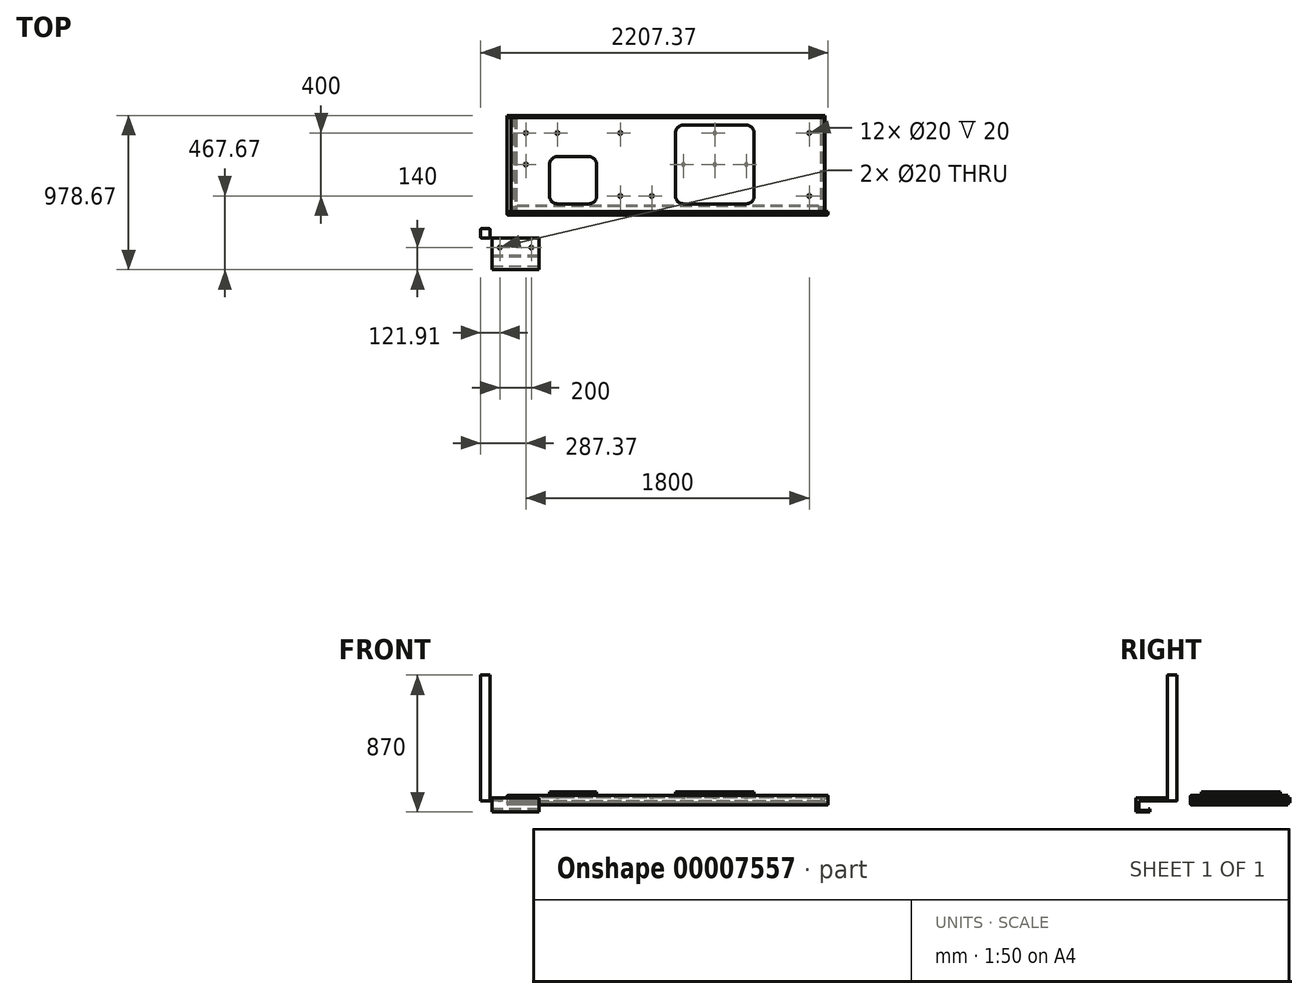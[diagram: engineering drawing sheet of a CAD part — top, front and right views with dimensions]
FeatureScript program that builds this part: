
annotation { "Feature Type Name" : "Feature", "Feature Type Description" : "" }
export const myFeature = defineFeature(function(context is Context, id is Id, definition is map)
    precondition{}
    {
        {
            var Q0;
            Q0=qCreatedBy(makeId("Top.planeOp"),FACE);
            var sketch = newSketch(context, id + "F0", { "sketchPlane" : qUnion([Q0])});
            skLineSegment(sketch, "E0.bottom", {"start": v(-63.9, 60.76) * mm, "end": v(-19.9, 60.76) * mm});
            skLineSegment(sketch, "E0.top", {"start": v(-63.9, 0.76) * mm, "end": v(-19.9, 0.76) * mm});
            skLineSegment(sketch, "E0.left", {"start": v(-71.9, 52.76) * mm, "end": v(-71.9, 8.76) * mm});
            skLineSegment(sketch, "E0.right", {"start": v(-11.9, 52.76) * mm, "end": v(-11.9, 8.76) * mm});
            skPoint(sketch, "E1.visualSharp", {"position": v(-71.9, 60.76) * mm});
            skArc(sketch, "E1.filletArc", {"start": v(-63.9, 60.76) * mm, "mid": v(-69.56, 58.42) * mm, "end": v(-71.9, 52.76) * mm});
            skPoint(sketch, "E2.visualSharp", {"position": v(-11.9, 0.76) * mm});
            skArc(sketch, "E2.filletArc", {"start": v(-19.9, 0.76) * mm, "mid": v(-14.25, 3.1) * mm, "end": v(-11.9, 8.76) * mm});
            skPoint(sketch, "E3.visualSharp", {"position": v(-71.9, 0.76) * mm});
            skArc(sketch, "E3.filletArc", {"start": v(-71.9, 8.76) * mm, "mid": v(-69.56, 3.1) * mm, "end": v(-63.9, 0.76) * mm});
            skPoint(sketch, "E4.visualSharp", {"position": v(-11.9, 60.76) * mm});
            skArc(sketch, "E4.filletArc", {"start": v(-11.9, 52.76) * mm, "mid": v(-14.25, 58.42) * mm, "end": v(-19.9, 60.76) * mm});
            skSolve(sketch);
        }
        {
            var Q0;
            Q0=makeQuery(id+"F0.imprint","IMPRINT",FACE,{"disambiguationData":[TD([[makeQuery(id+"F0.imprint","IMPRINT",EDGE,{"derivedFrom":sQuery(id+"F0.wireOp",EDGE,"E0.bottom")}),-1.0]])]});
            extrude(context, id + "F1", {"entities" : qUnion([Q0]), "depth" : 800 * mm});
        }
        {
            var Q0;
            Q0=qCreatedBy(makeId("Top.planeOp"),FACE);
            var sketch = newSketch(context, id + "F2", { "sketchPlane" : qUnion([Q0])});
            skLineSegment(sketch, "E5.bottom", {"start": v(114.46, 147.67) * mm, "end": v(2116.46, 147.67) * mm});
            skLineSegment(sketch, "E5.top", {"start": v(114.46, 787.67) * mm, "end": v(2116.46, 787.67) * mm});
            skLineSegment(sketch, "E5.left", {"start": v(114.46, 147.67) * mm, "end": v(114.46, 787.67) * mm});
            skLineSegment(sketch, "E5.right", {"start": v(2116.46, 147.67) * mm, "end": v(2116.46, 787.67) * mm});
            skSolve(sketch);
        }
        {
            var Q0;
            Q0=makeQuery(id+"F2.imprint","IMPRINT",FACE,{"disambiguationData":[TD([[makeQuery(id+"F2.imprint","IMPRINT",EDGE,{"derivedFrom":sQuery(id+"F2.wireOp",EDGE,"E5.bottom")}),1.0]])]});
            extrude(context, id + "F3", {"entities" : qUnion([Q0]), "depth" : 35 * mm});
        }
        {
            var Q0;
            Q0=makeQuery(id+"F3.opExtrude","CAP_FACE",FACE,{"disambiguationData":[OSD([sQuery(id+"F2.wireOp",EDGE,"E5.bottom"),sQuery(id+"F2.wireOp",EDGE,"E5.top"),sQuery(id+"F2.wireOp",EDGE,"E5.left"),sQuery(id+"F2.wireOp",EDGE,"E5.right")])],"isStart":false});
            var sketch = newSketch(context, id + "F4", { "sketchPlane" : qUnion([Q0])});
            skPoint(sketch, "E6", {"position": v(215.46, 267.67) * mm});
            skPoint(sketch, "E7.0.1.0", {"position": v(215.46, 467.67) * mm});
            skPoint(sketch, "E7.0.2.0", {"position": v(215.46, 667.67) * mm});
            skPoint(sketch, "E7.1.0.0", {"position": v(415.46, 267.67) * mm});
            skPoint(sketch, "E7.1.1.0", {"position": v(415.46, 467.67) * mm});
            skPoint(sketch, "E7.1.2.0", {"position": v(415.46, 667.67) * mm});
            skPoint(sketch, "E7.2.0.0", {"position": v(615.46, 267.67) * mm});
            skPoint(sketch, "E7.2.1.0", {"position": v(615.46, 467.67) * mm});
            skPoint(sketch, "E7.2.2.0", {"position": v(615.46, 667.67) * mm});
            skPoint(sketch, "E7.3.0.0", {"position": v(815.46, 267.67) * mm});
            skPoint(sketch, "E7.3.1.0", {"position": v(815.46, 467.67) * mm});
            skPoint(sketch, "E7.3.2.0", {"position": v(815.46, 667.67) * mm});
            skPoint(sketch, "E7.4.0.0", {"position": v(1015.46, 267.67) * mm});
            skPoint(sketch, "E7.4.1.0", {"position": v(1015.46, 467.67) * mm});
            skPoint(sketch, "E7.4.2.0", {"position": v(1015.46, 667.67) * mm});
            skPoint(sketch, "E7.5.0.0", {"position": v(1215.46, 267.67) * mm});
            skPoint(sketch, "E7.5.1.0", {"position": v(1215.46, 467.67) * mm});
            skPoint(sketch, "E7.5.2.0", {"position": v(1215.46, 667.67) * mm});
            skPoint(sketch, "E7.6.0.0", {"position": v(1415.46, 267.67) * mm});
            skPoint(sketch, "E7.6.1.0", {"position": v(1415.46, 467.67) * mm});
            skPoint(sketch, "E7.6.2.0", {"position": v(1415.46, 667.67) * mm});
            skPoint(sketch, "E7.7.0.0", {"position": v(1615.46, 267.67) * mm});
            skPoint(sketch, "E7.7.1.0", {"position": v(1615.46, 467.67) * mm});
            skPoint(sketch, "E7.7.2.0", {"position": v(1615.46, 667.67) * mm});
            skPoint(sketch, "E7.8.0.0", {"position": v(1815.46, 267.67) * mm});
            skPoint(sketch, "E7.8.1.0", {"position": v(1815.46, 467.67) * mm});
            skPoint(sketch, "E7.8.2.0", {"position": v(1815.46, 667.67) * mm});
            skPoint(sketch, "E7.9.0.0", {"position": v(2015.46, 267.67) * mm});
            skPoint(sketch, "E7.9.1.0", {"position": v(2015.46, 467.67) * mm});
            skPoint(sketch, "E7.9.2.0", {"position": v(2015.46, 667.67) * mm});
            skLineSegment(sketch, "E7.direction1", {"start": v(215.46, 267.67) * mm, "end": v(415.46, 267.67) * mm, "construction": true});
            skLineSegment(sketch, "E7.direction2", {"start": v(215.46, 267.67) * mm, "end": v(215.46, 467.67) * mm, "construction": true});
            skCircle(sketch, "E8", {"center": v(415.46, 467.67) * mm, "radius": 10 * mm});
            skCircle(sketch, "E9", {"center": v(615.46, 467.67) * mm, "radius": 10 * mm});
            skCircle(sketch, "E10", {"center": v(415.46, 267.67) * mm, "radius": 10 * mm});
            skCircle(sketch, "E11", {"center": v(615.46, 267.67) * mm, "radius": 10 * mm});
            skPoint(sketch, "E12.0.0.3", {"position": v(215.46, 867.67) * mm});
            skPoint(sketch, "E12.0.1.3", {"position": v(415.46, 867.67) * mm});
            skPoint(sketch, "E12.0.2.3", {"position": v(615.46, 867.67) * mm});
            skPoint(sketch, "E12.0.3.3", {"position": v(815.46, 867.67) * mm});
            skPoint(sketch, "E12.0.4.3", {"position": v(1015.46, 867.67) * mm});
            skPoint(sketch, "E12.0.5.3", {"position": v(1215.46, 867.67) * mm});
            skPoint(sketch, "E12.0.6.3", {"position": v(1415.46, 867.67) * mm});
            skPoint(sketch, "E12.0.7.3", {"position": v(1615.46, 867.67) * mm});
            skPoint(sketch, "E12.0.8.3", {"position": v(1815.46, 867.67) * mm});
            skPoint(sketch, "E12.0.9.3", {"position": v(2015.46, 867.67) * mm});
            skCircle(sketch, "E13", {"center": v(415.46, 867.67) * mm, "radius": 10 * mm});
            skCircle(sketch, "E14", {"center": v(815.46, 267.67) * mm, "radius": 10 * mm});
            skCircle(sketch, "E15", {"center": v(815.46, 667.67) * mm, "radius": 10 * mm});
            skCircle(sketch, "E16", {"center": v(1215.46, 667.67) * mm, "radius": 10 * mm});
            skCircle(sketch, "E17", {"center": v(1215.46, 267.67) * mm, "radius": 10 * mm});
            skCircle(sketch, "E18", {"center": v(1215.46, 467.67) * mm, "radius": 10 * mm});
            skCircle(sketch, "E19", {"center": v(1415.46, 467.67) * mm, "radius": 10 * mm});
            skCircle(sketch, "E20", {"center": v(1615.46, 467.67) * mm, "radius": 10 * mm});
            skCircle(sketch, "E21", {"center": v(1415.46, 667.67) * mm, "radius": 10 * mm});
            skCircle(sketch, "E22", {"center": v(1615.46, 667.67) * mm, "radius": 10 * mm});
            skCircle(sketch, "E23", {"center": v(2015.46, 667.67) * mm, "radius": 10 * mm});
            skCircle(sketch, "E24", {"center": v(1615.46, 267.67) * mm, "radius": 10 * mm});
            skCircle(sketch, "E25", {"center": v(2015.46, 267.67) * mm, "radius": 10 * mm});
            skCircle(sketch, "E26", {"center": v(215.46, 667.67) * mm, "radius": 10 * mm});
            skCircle(sketch, "E27", {"center": v(215.46, 467.67) * mm, "radius": 10 * mm});
            skCircle(sketch, "E28", {"center": v(415.46, 667.67) * mm, "radius": 10 * mm});
            skCircle(sketch, "E29", {"center": v(1015.46, 267.67) * mm, "radius": 10 * mm});
            skSolve(sketch);
        }
        {
            var Q0;
            Q0 = qSketchRegion(id + "F4", true);
            extrude(context, id + "F5", {"entities" : qUnion([Q0]), "operationType" : NewBodyOperationType.REMOVE, "oppositeDirection" : true, "depth" : 20 * mm});
        }
        {
            var Q0;
            Q0=makeQuery(id+"F3.opExtrude","SWEPT_FACE",FACE,{"disambiguationData":[OSD([sQuery(id+"F2.wireOp",EDGE,"E5.bottom")])]});
            var sketch = newSketch(context, id + "F6", { "sketchPlane" : qUnion([Q0])});
            skLineSegment(sketch, "E30.bottom", {"start": v(114.46, 35) * mm, "end": v(120.46, 35) * mm});
            skLineSegment(sketch, "E30.top", {"start": v(114.46, 23) * mm, "end": v(120.46, 23) * mm});
            skLineSegment(sketch, "E30.left", {"start": v(114.46, 35) * mm, "end": v(114.46, 23) * mm});
            skLineSegment(sketch, "E30.right", {"start": v(120.46, 35) * mm, "end": v(120.46, 23) * mm});
            skLineSegment(sketch, "E31.bottom", {"start": v(114.46, 0) * mm, "end": v(120.46, 0) * mm});
            skLineSegment(sketch, "E31.top", {"start": v(114.46, 11) * mm, "end": v(120.46, 11) * mm});
            skLineSegment(sketch, "E31.left", {"start": v(114.46, 0) * mm, "end": v(114.46, 11) * mm});
            skLineSegment(sketch, "E31.right", {"start": v(120.46, 0) * mm, "end": v(120.46, 11) * mm});
            skLineSegment(sketch, "E32.bottom", {"start": v(132.46, 0) * mm, "end": v(144.46, 0) * mm});
            skLineSegment(sketch, "E32.top", {"start": v(132.46, 6) * mm, "end": v(144.46, 6) * mm});
            skLineSegment(sketch, "E32.left", {"start": v(132.46, 0) * mm, "end": v(132.46, 6) * mm});
            skLineSegment(sketch, "E32.right", {"start": v(144.46, 0) * mm, "end": v(144.46, 6) * mm});
            skLineSegment(sketch, "E33.bottom", {"start": v(2116.46, 35) * mm, "end": v(2110.46, 35) * mm});
            skLineSegment(sketch, "E33.top", {"start": v(2116.46, 23) * mm, "end": v(2110.46, 23) * mm});
            skLineSegment(sketch, "E33.left", {"start": v(2116.46, 35) * mm, "end": v(2116.46, 23) * mm});
            skLineSegment(sketch, "E33.right", {"start": v(2110.46, 35) * mm, "end": v(2110.46, 23) * mm});
            skLineSegment(sketch, "E34.bottom", {"start": v(2116.46, 0) * mm, "end": v(2110.46, 0) * mm});
            skLineSegment(sketch, "E34.top", {"start": v(2116.46, 11) * mm, "end": v(2110.46, 11) * mm});
            skLineSegment(sketch, "E34.left", {"start": v(2116.46, 0) * mm, "end": v(2116.46, 11) * mm});
            skLineSegment(sketch, "E34.right", {"start": v(2110.46, 0) * mm, "end": v(2110.46, 11) * mm});
            skLineSegment(sketch, "E35.bottom", {"start": v(2098.46, 0) * mm, "end": v(2086.46, 0) * mm});
            skLineSegment(sketch, "E35.top", {"start": v(2098.46, 6) * mm, "end": v(2086.46, 6) * mm});
            skLineSegment(sketch, "E35.left", {"start": v(2098.46, 0) * mm, "end": v(2098.46, 6) * mm});
            skLineSegment(sketch, "E35.right", {"start": v(2086.46, 0) * mm, "end": v(2086.46, 6) * mm});
            skSolve(sketch);
        }
        {
            var Q0;
            Q0 = qSketchRegion(id + "F6", true);
            extrude(context, id + "F7", {"entities" : qUnion([Q0]), "operationType" : NewBodyOperationType.REMOVE, "endBound" : BoundingType.UP_TO_NEXT, "oppositeDirection" : true, "depth" : 25 * mm});
        }
        {
            var Q0;
            Q0=makeQuery(id+"F3.opExtrude","CAP_FACE",FACE,{"disambiguationData":[OSD([sQuery(id+"F2.wireOp",EDGE,"E5.bottom"),sQuery(id+"F2.wireOp",EDGE,"E5.top"),sQuery(id+"F2.wireOp",EDGE,"E5.left"),sQuery(id+"F2.wireOp",EDGE,"E5.right")])],"isStart":false});
            var sketch = newSketch(context, id + "F8", { "sketchPlane" : qUnion([Q0])});
            skLineSegment(sketch, "E36", {"start": v(415.46, 517.67) * mm, "end": v(615.46, 517.67) * mm});
            skArc(sketch, "E37", {"start": v(615.46, 517.67) * mm, "mid": v(650.82, 503.03) * mm, "end": v(665.46, 467.67) * mm});
            skLineSegment(sketch, "E38", {"start": v(665.46, 467.67) * mm, "end": v(665.46, 267.67) * mm});
            skArc(sketch, "E39", {"start": v(665.46, 267.67) * mm, "mid": v(650.82, 232.31) * mm, "end": v(615.46, 217.67) * mm});
            skLineSegment(sketch, "E40", {"start": v(615.46, 217.67) * mm, "end": v(415.46, 217.67) * mm});
            skArc(sketch, "E41", {"start": v(415.46, 217.67) * mm, "mid": v(380.1, 232.31) * mm, "end": v(365.46, 267.67) * mm});
            skLineSegment(sketch, "E42", {"start": v(365.46, 267.67) * mm, "end": v(365.46, 467.67) * mm});
            skArc(sketch, "E43", {"start": v(365.46, 467.67) * mm, "mid": v(380.1, 503.03) * mm, "end": v(415.46, 517.67) * mm});
            skLineSegment(sketch, "E44.bottom", {"start": v(1215.46, 717.67) * mm, "end": v(1615.46, 717.67) * mm});
            skLineSegment(sketch, "E44.top", {"start": v(1215.46, 217.67) * mm, "end": v(1615.46, 217.67) * mm});
            skLineSegment(sketch, "E44.left", {"start": v(1165.46, 667.67) * mm, "end": v(1165.46, 267.67) * mm});
            skLineSegment(sketch, "E44.right", {"start": v(1665.46, 667.67) * mm, "end": v(1665.46, 267.67) * mm});
            skPoint(sketch, "E45.visualSharp", {"position": v(1165.46, 717.67) * mm});
            skArc(sketch, "E45.filletArc", {"start": v(1215.46, 717.67) * mm, "mid": v(1180.1, 703.03) * mm, "end": v(1165.46, 667.67) * mm});
            skPoint(sketch, "E46.visualSharp", {"position": v(1665.46, 717.67) * mm});
            skArc(sketch, "E46.filletArc", {"start": v(1665.46, 667.67) * mm, "mid": v(1650.82, 703.03) * mm, "end": v(1615.46, 717.67) * mm});
            skPoint(sketch, "E47.visualSharp", {"position": v(1665.46, 217.67) * mm});
            skArc(sketch, "E47.filletArc", {"start": v(1615.46, 217.67) * mm, "mid": v(1650.82, 232.31) * mm, "end": v(1665.46, 267.67) * mm});
            skPoint(sketch, "E48.visualSharp", {"position": v(1165.46, 217.67) * mm});
            skArc(sketch, "E48.filletArc", {"start": v(1165.46, 267.67) * mm, "mid": v(1180.1, 232.31) * mm, "end": v(1215.46, 217.67) * mm});
            skSolve(sketch);
        }
        {
            var Q0;
            Q0 = qSketchRegion(id + "F8", true);
            extrude(context, id + "F9", {"entities" : qUnion([Q0]), "depth" : 21 * mm});
        }
        {
            var Q0;
            Q0=makeQuery(id+"F4.imprint","IMPRINT",FACE,{"disambiguationData":[TD([[makeQuery(id+"F4.imprint","IMPRINT",EDGE,{"derivedFrom":sQuery(id+"F4.wireOp",EDGE,"E8")}),1.0]])]});
            var Q1;
            Q1=makeQuery(id+"F4.imprint","IMPRINT",FACE,{"disambiguationData":[TD([[makeQuery(id+"F4.imprint","IMPRINT",EDGE,{"derivedFrom":sQuery(id+"F4.wireOp",EDGE,"E9")}),1.0]])]});
            var Q2;
            Q2=makeQuery(id+"F4.imprint","IMPRINT",FACE,{"disambiguationData":[TD([[makeQuery(id+"F4.imprint","IMPRINT",EDGE,{"derivedFrom":sQuery(id+"F4.wireOp",EDGE,"E11")}),1.0]])]});
            var Q3;
            Q3=makeQuery(id+"F4.imprint","IMPRINT",FACE,{"disambiguationData":[TD([[makeQuery(id+"F4.imprint","IMPRINT",EDGE,{"derivedFrom":sQuery(id+"F4.wireOp",EDGE,"E10")}),1.0]])]});
            var Q4;
            Q4=makeQuery(id+"F4.imprint","IMPRINT",FACE,{"disambiguationData":[TD([[makeQuery(id+"F4.imprint","IMPRINT",EDGE,{"derivedFrom":sQuery(id+"F4.wireOp",EDGE,"E16")}),1.0]])]});
            var Q5;
            Q5=makeQuery(id+"F4.imprint","IMPRINT",FACE,{"disambiguationData":[TD([[makeQuery(id+"F4.imprint","IMPRINT",EDGE,{"derivedFrom":sQuery(id+"F4.wireOp",EDGE,"E22")}),1.0]])]});
            var Q6;
            Q6=makeQuery(id+"F4.imprint","IMPRINT",FACE,{"disambiguationData":[TD([[makeQuery(id+"F4.imprint","IMPRINT",EDGE,{"derivedFrom":sQuery(id+"F4.wireOp",EDGE,"E17")}),1.0]])]});
            var Q7;
            Q7=makeQuery(id+"F4.imprint","IMPRINT",FACE,{"disambiguationData":[TD([[makeQuery(id+"F4.imprint","IMPRINT",EDGE,{"derivedFrom":sQuery(id+"F4.wireOp",EDGE,"E24")}),1.0]])]});
            var Q8;
            Q8=sQuery(id+"F4.wireOp",EDGE,"E8");
            extrude(context, id + "F10", {"entities" : qUnion([Q0, Q1, Q2, Q3, Q4, Q5, Q6, Q7]), "operationType" : NewBodyOperationType.ADD, "surfaceEntities" : qUnion([Q8]), "oppositeDirection" : true, "depth" : 20 * mm});
        }
        {
            var Q0;
            Q0=makeQuery(id+"F3.opExtrude","SWEPT_FACE",FACE,{"disambiguationData":[OSD([sQuery(id+"F2.wireOp",EDGE,"E5.bottom")])]});
            var sketch = newSketch(context, id + "F11", { "sketchPlane" : qUnion([Q0])});
            skLineSegment(sketch, "E49", {"start": v(120.46, 35) * mm, "end": v(95.46, 35) * mm});
            skLineSegment(sketch, "E50", {"start": v(95.46, 35) * mm, "end": v(95.46, -25) * mm});
            skLineSegment(sketch, "E51", {"start": v(95.46, -25) * mm, "end": v(155.46, -25) * mm});
            skLineSegment(sketch, "E52", {"start": v(155.46, -8) * mm, "end": v(147.46, -8) * mm});
            skLineSegment(sketch, "E53", {"start": v(147.46, -8) * mm, "end": v(147.46, -16) * mm});
            skLineSegment(sketch, "E54", {"start": v(147.46, -16) * mm, "end": v(155.46, -16) * mm});
            skLineSegment(sketch, "E55", {"start": v(155.46, 0) * mm, "end": v(155.46, -8) * mm});
            skLineSegment(sketch, "E56", {"start": v(155.46, -16) * mm, "end": v(155.46, -25) * mm});
            skLineSegment(sketch, "E57", {"start": v(120.46, 35) * mm, "end": v(120.46, 23) * mm});
            skLineSegment(sketch, "E58", {"start": v(120.46, 23) * mm, "end": v(114.46, 23) * mm});
            skLineSegment(sketch, "E59", {"start": v(114.46, 23) * mm, "end": v(114.46, 11) * mm});
            skLineSegment(sketch, "E60", {"start": v(114.46, 11) * mm, "end": v(120.46, 11) * mm});
            skLineSegment(sketch, "E61", {"start": v(120.46, 11) * mm, "end": v(120.46, 0) * mm});
            skLineSegment(sketch, "E62", {"start": v(120.46, 0) * mm, "end": v(132.46, 0) * mm});
            skLineSegment(sketch, "E63", {"start": v(132.46, 6) * mm, "end": v(144.46, 6) * mm});
            skLineSegment(sketch, "E64", {"start": v(144.46, 6) * mm, "end": v(144.46, 0) * mm});
            skLineSegment(sketch, "E65", {"start": v(144.46, 0) * mm, "end": v(155.46, 0) * mm});
            skLineSegment(sketch, "E66", {"start": v(132.46, 6) * mm, "end": v(132.46, 0) * mm});
            skSolve(sketch);
        }
        {
            var Q0;
            Q0=makeQuery(id+"F11.imprint","IMPRINT",FACE,{"disambiguationData":[TD([[makeQuery(id+"F11.imprint","IMPRINT",EDGE,{"derivedFrom":sQuery(id+"F11.wireOp",EDGE,"E49")}),1.0]])]});
            var Q1;
            {var subQ0=sQuery(id+"F11.wireOp",EDGE,"undLv0iN-hPa5-GqhO-h3vo-g1M268CYv5Xv");Q1=makeQuery(id+"F11.imprint","IMPRINT",FACE,{"disambiguationData":[TD([[makeQuery(id+"F11.imprint","IMPRINT",EDGE,{"derivedFrom":subQ0}),-1.0]])]});}
            var Q2;
            Q2=makeQuery(id+"F11.imprint","IMPRINT",FACE,{"disambiguationData":[TD([[makeQuery(id+"F11.imprint","IMPRINT",EDGE,{"derivedFrom":sQuery(id+"F11.wireOp",EDGE,"E63")}),-1.0]])]});
            var Q3;
            Q3=makeQuery(id+"F3.opExtrude","SWEPT_FACE",FACE,{"disambiguationData":[OSD([sQuery(id+"F2.wireOp",EDGE,"E5.top")])]});
            extrude(context, id + "F12", {"entities" : qUnion([Q0, Q1, Q2]), "endBound" : BoundingType.UP_TO_SURFACE, "oppositeDirection" : true, "endBoundEntityFace" : qUnion([Q3]), "depth" : 650 * mm});
        }
        {
            var Q0;
            Q0=makeQuery(id+"F12.opExtrude","CAP_FACE",FACE,{"disambiguationData":[OSD([sQuery(id+"F11.wireOp",EDGE,"E49"),sQuery(id+"F11.wireOp",EDGE,"E50"),sQuery(id+"F11.wireOp",EDGE,"E51"),sQuery(id+"F11.wireOp",EDGE,"E52"),sQuery(id+"F11.wireOp",EDGE,"E53"),sQuery(id+"F11.wireOp",EDGE,"E54"),sQuery(id+"F11.wireOp",EDGE,"E55"),sQuery(id+"F11.wireOp",EDGE,"E56"),sQuery(id+"F11.wireOp",EDGE,"E57"),sQuery(id+"F11.wireOp",EDGE,"E58"),sQuery(id+"F11.wireOp",EDGE,"E59"),sQuery(id+"F11.wireOp",EDGE,"E60"),sQuery(id+"F11.wireOp",EDGE,"E61"),sQuery(id+"F11.wireOp",EDGE,"E62"),sQuery(id+"F11.wireOp",EDGE,"E63"),sQuery(id+"F11.wireOp",EDGE,"E64"),sQuery(id+"F11.wireOp",EDGE,"E65"),sQuery(id+"F11.wireOp",EDGE,"E66")])],"isStart":true});
            var sketch = newSketch(context, id + "F13", { "sketchPlane" : qUnion([Q0])});
            skLineSegment(sketch, "E67", {"start": v(155.46, 0) * mm, "end": v(155.46, -8) * mm});
            skLineSegment(sketch, "E68", {"start": v(155.46, -8) * mm, "end": v(147.46, -8) * mm});
            skLineSegment(sketch, "E69", {"start": v(147.46, -8) * mm, "end": v(147.46, -16) * mm});
            skLineSegment(sketch, "E70", {"start": v(147.46, -16) * mm, "end": v(155.46, -16) * mm});
            skLineSegment(sketch, "E71", {"start": v(155.46, -16) * mm, "end": v(155.46, -25) * mm});
            skLineSegment(sketch, "E72", {"start": v(155.46, -25) * mm, "end": v(2075.46, -25) * mm});
            skPoint(sketch, "E72.endSnap0", {"position": v(125.46, -25) * mm});
            skLineSegment(sketch, "E73", {"start": v(2075.46, -25) * mm, "end": v(2075.46, -16) * mm});
            skLineSegment(sketch, "E74", {"start": v(2075.46, -16) * mm, "end": v(2083.46, -16) * mm});
            skLineSegment(sketch, "E75", {"start": v(2083.46, -16) * mm, "end": v(2083.46, -8) * mm});
            skLineSegment(sketch, "E76", {"start": v(2083.46, -8) * mm, "end": v(2075.46, -8) * mm});
            skLineSegment(sketch, "E77", {"start": v(2075.46, -8) * mm, "end": v(2075.46, 0) * mm});
            skLineSegment(sketch, "E78", {"start": v(2075.46, 0) * mm, "end": v(155.46, 0) * mm});
            skLineSegment(sketch, "E79", {"start": v(120.46, 0) * mm, "end": v(155.46, -35) * mm, "construction": true});
            skLineSegment(sketch, "E80", {"start": v(147.46, -16) * mm, "end": v(147.46, -27) * mm, "construction": true});
            skLineSegment(sketch, "E81", {"start": v(147.46, -27) * mm, "end": v(2083.46, -27) * mm, "construction": true});
            skLineSegment(sketch, "E82", {"start": v(2110.46, 0) * mm, "end": v(2075.46, -35) * mm, "construction": true});
            skLineSegment(sketch, "E83", {"start": v(2083.46, -16) * mm, "end": v(2083.46, -27) * mm, "construction": true});
            skSolve(sketch);
        }
        {
            var Q0;
            Q0 = qSketchRegion(id + "F13", true);
            extrude(context, id + "F14", {"entities" : qUnion([Q0]), "oppositeDirection" : true, "depth" : 60 * mm});
        }
        {
            var Q0;
            Q0=qCreatedBy(makeId("Right.planeOp"),FACE);
            var sketch = newSketch(context, id + "F15", { "sketchPlane" : qUnion([Q0])});
            skLineSegment(sketch, "E84", {"start": v(-180, 0) * mm, "end": v(-180, -60) * mm});
            skLineSegment(sketch, "E85", {"start": v(-180, -60) * mm, "end": v(-120, -60) * mm});
            skLineSegment(sketch, "E86", {"start": v(-120, -60) * mm, "end": v(-120, -50) * mm});
            skLineSegment(sketch, "E87", {"start": v(-120, -50) * mm, "end": v(-110, -50) * mm});
            skLineSegment(sketch, "E88", {"start": v(-110, -50) * mm, "end": v(-110, -70) * mm});
            skLineSegment(sketch, "E89", {"start": v(-110, -70) * mm, "end": v(-200, -70) * mm});
            skLineSegment(sketch, "E90", {"start": v(-200, -70) * mm, "end": v(-200, 20) * mm});
            skLineSegment(sketch, "E91", {"start": v(-200, 20) * mm, "end": v(0, 20) * mm});
            skLineSegment(sketch, "E92", {"start": v(0, 20) * mm, "end": v(0, 0) * mm});
            skLineSegment(sketch, "E93", {"start": v(0, 0) * mm, "end": v(-180, 0) * mm});
            skSolve(sketch);
        }
        {
            var Q0;
            Q0 = qSketchRegion(id + "F15", true);
            extrude(context, id + "F16", {"entities" : qUnion([Q0]), "depth" : 300 * mm});
        }
        {
            var Q0;
            Q0=makeQuery(id+"F16.opExtrude","SWEPT_FACE",FACE,{"disambiguationData":[OSD([sQuery(id+"F15.wireOp",EDGE,"E93")])]});
            var sketch = newSketch(context, id + "F17", { "sketchPlane" : qUnion([Q0])});
            skLineSegment(sketch, "E94", {"start": v(300, 60) * mm, "end": v(0, 60) * mm, "construction": true});
            skCircle(sketch, "E95", {"center": v(250, 60) * mm, "radius": 10 * mm});
            skCircle(sketch, "E96", {"center": v(50, 60) * mm, "radius": 10 * mm});
            skSolve(sketch);
        }
        {
            var Q0;
            Q0 = qSketchRegion(id + "F17", true);
            extrude(context, id + "F18", {"entities" : qUnion([Q0]), "operationType" : NewBodyOperationType.REMOVE, "endBound" : BoundingType.UP_TO_NEXT, "oppositeDirection" : true, "depth" : 25 * mm});
        }
        {
            var Q0;
            Q0=makeQuery(id+"F12.opExtrude","SWEPT_FACE",FACE,{"disambiguationData":[OSD([sQuery(id+"F11.wireOp",EDGE,"E50")])]});
            var sketch = newSketch(context, id + "F19", { "sketchPlane" : qUnion([Q0])});
            skLineSegment(sketch, "E97", {"start": v(-168.67, 35) * mm, "end": v(-168.67, 20) * mm});
            skLineSegment(sketch, "E98", {"start": v(-168.67, 20) * mm, "end": v(-156.67, 23) * mm});
            skLineSegment(sketch, "E99", {"start": v(-156.67, 23) * mm, "end": v(-156.67, -13) * mm});
            skLineSegment(sketch, "E100", {"start": v(-156.67, -13) * mm, "end": v(-168.67, -10) * mm});
            skLineSegment(sketch, "E101", {"start": v(-168.67, -10) * mm, "end": v(-168.67, -25) * mm});
            skLineSegment(sketch, "E102", {"start": v(-168.67, -25) * mm, "end": v(-147.67, -25) * mm});
            skLineSegment(sketch, "E103", {"start": v(-147.67, -25) * mm, "end": v(-147.67, 35) * mm});
            skLineSegment(sketch, "E104", {"start": v(-147.67, 35) * mm, "end": v(-168.67, 35) * mm});
            skLineSegment(sketch, "E105", {"start": v(-467.67, 35) * mm, "end": v(-467.67, -25) * mm, "construction": true});
            skLineSegment(sketch, "E106.MirrorCS", {"start": v(-766.67, 20) * mm, "end": v(-778.67, 23) * mm});
            skLineSegment(sketch, "E107.MirrorCS", {"start": v(-766.67, 35) * mm, "end": v(-766.67, 20) * mm});
            skLineSegment(sketch, "E108.MirrorCS", {"start": v(-778.67, -13) * mm, "end": v(-766.67, -10) * mm});
            skLineSegment(sketch, "E109.MirrorCS", {"start": v(-766.67, -10) * mm, "end": v(-766.67, -25) * mm});
            skLineSegment(sketch, "E110.MirrorCS", {"start": v(-787.67, 35) * mm, "end": v(-766.67, 35) * mm});
            skLineSegment(sketch, "E111.MirrorCS", {"start": v(-766.67, -25) * mm, "end": v(-787.67, -25) * mm});
            skLineSegment(sketch, "E112.MirrorCS", {"start": v(-778.67, 23) * mm, "end": v(-778.67, -13) * mm});
            skLineSegment(sketch, "E113.MirrorCS", {"start": v(-787.67, -25) * mm, "end": v(-787.67, 35) * mm});
            skSolve(sketch);
        }
        {
            var Q0;
            Q0=makeQuery(id+"F19.imprint","IMPRINT",FACE,{"disambiguationData":[TD([[makeQuery(id+"F19.imprint","IMPRINT",EDGE,{"derivedFrom":sQuery(id+"F19.wireOp",EDGE,"E97")}),1.0]])]});
            var Q1;
            Q1=makeQuery(id+"F19.imprint","IMPRINT",FACE,{"disambiguationData":[TD([[makeQuery(id+"F19.imprint","IMPRINT",EDGE,{"derivedFrom":sQuery(id+"F19.wireOp",EDGE,"E106.MirrorCS")}),-1.0]])]});
            extrude(context, id + "F20", {"entities" : qUnion([Q0, Q1]), "operationType" : NewBodyOperationType.REMOVE, "oppositeDirection" : true, "depth" : 2100 * mm});
        }
        {
            var Q0;
            Q0=makeQuery(id+"F19.imprint","IMPRINT",FACE,{"disambiguationData":[TD([[makeQuery(id+"F19.imprint","IMPRINT",EDGE,{"derivedFrom":sQuery(id+"F19.wireOp",EDGE,"E97")}),1.0]])]});
            extrude(context, id + "F21", {"entities" : qUnion([Q0]), "oppositeDirection" : true, "depth" : 2040 * mm});
        }
        {
            assignVariable(context, id + "F22", {"name" : "rounding_radius", "anyValue" : 6});
        }
        {
            var Q0;
            Q0=makeQuery(id+"F12.opExtrude","SWEPT_EDGE",EDGE,{"disambiguationData":[OSD([sQuery(id+"F11.wireOp",EDGE,"E49"),sQuery(id+"F11.wireOp",EDGE,"E50")])]});
            var Q1;
            Q1=makeQuery(id+"F12.opExtrude","SWEPT_EDGE",EDGE,{"disambiguationData":[OSD([sQuery(id+"F11.wireOp",EDGE,"E50"),sQuery(id+"F11.wireOp",EDGE,"E51")])]});
            fillet(context, id + "F23", {"entities" : qUnion([Q0, Q1]), "radius" : (getVariable(context, 'rounding_radius')) * mm, "allowEdgeOverflow" : false});
        }
        {
            var Q0;
            Q0=makeQuery(id+"F21.opExtrude","CAP_EDGE",EDGE,{"disambiguationData":[OSD([sQuery(id+"F19.wireOp",EDGE,"E103")])],"isStart":true});
            var Q1;
            Q1=makeQuery(id+"F21.opExtrude","CAP_EDGE",EDGE,{"disambiguationData":[OSD([sQuery(id+"F19.wireOp",EDGE,"E103")])],"isStart":false});
            fillet(context, id + "F24", {"entities" : qUnion([Q0, Q1]), "radius" : (getVariable(context, 'rounding_radius')) * mm, "tangentPropagation" : true, "allowEdgeOverflow" : false});
        }
        {
            var Q0;
            Q0=makeQuery(id+"F21.opExtrude","SWEPT_EDGE",EDGE,{"disambiguationData":[OSD([sQuery(id+"F19.wireOp",EDGE,"E103"),sQuery(id+"F19.wireOp",EDGE,"E104")])]});
            var Q1;
            Q1=makeQuery(id+"F21.opExtrude","SWEPT_EDGE",EDGE,{"disambiguationData":[OSD([sQuery(id+"F19.wireOp",EDGE,"E102"),sQuery(id+"F19.wireOp",EDGE,"E103")])]});
            fillet(context, id + "F25", {"entities" : qUnion([Q0, Q1]), "radius" : (getVariable(context, 'rounding_radius')) * mm, "tangentPropagation" : true, "allowEdgeOverflow" : false});
        }
        {
            var Q0;
            Q0=makeQuery(id+"F14.opExtrude","CAP_FACE",FACE,{"disambiguationData":[OSD([sQuery(id+"F13.wireOp",EDGE,"E67"),sQuery(id+"F13.wireOp",EDGE,"E68"),sQuery(id+"F13.wireOp",EDGE,"E69"),sQuery(id+"F13.wireOp",EDGE,"E70"),sQuery(id+"F13.wireOp",EDGE,"E71"),sQuery(id+"F13.wireOp",EDGE,"E72"),sQuery(id+"F13.wireOp",EDGE,"E73"),sQuery(id+"F13.wireOp",EDGE,"E74"),sQuery(id+"F13.wireOp",EDGE,"E75"),sQuery(id+"F13.wireOp",EDGE,"E76"),sQuery(id+"F13.wireOp",EDGE,"E77"),sQuery(id+"F13.wireOp",EDGE,"E78")])],"isStart":false});
            var sketch = newSketch(context, id + "F26", { "sketchPlane" : qUnion([Q0])});
            skLineSegment(sketch, "E114.bottom", {"start": v(-2083.46, -8) * mm, "end": v(-147.46, -8) * mm});
            skLineSegment(sketch, "E114.top", {"start": v(-2083.46, -16) * mm, "end": v(-147.46, -16) * mm});
            skLineSegment(sketch, "E114.left", {"start": v(-2083.46, -8) * mm, "end": v(-2083.46, -16) * mm});
            skLineSegment(sketch, "E114.right", {"start": v(-147.46, -8) * mm, "end": v(-147.46, -16) * mm});
            skSolve(sketch);
        }
        {
            var Q0;
            Q0 = qSketchRegion(id + "F26", true);
            extrude(context, id + "F27", {"entities" : qUnion([Q0]), "operationType" : NewBodyOperationType.REMOVE, "oppositeDirection" : true, "depth" : 8 * mm});
        }
    });
